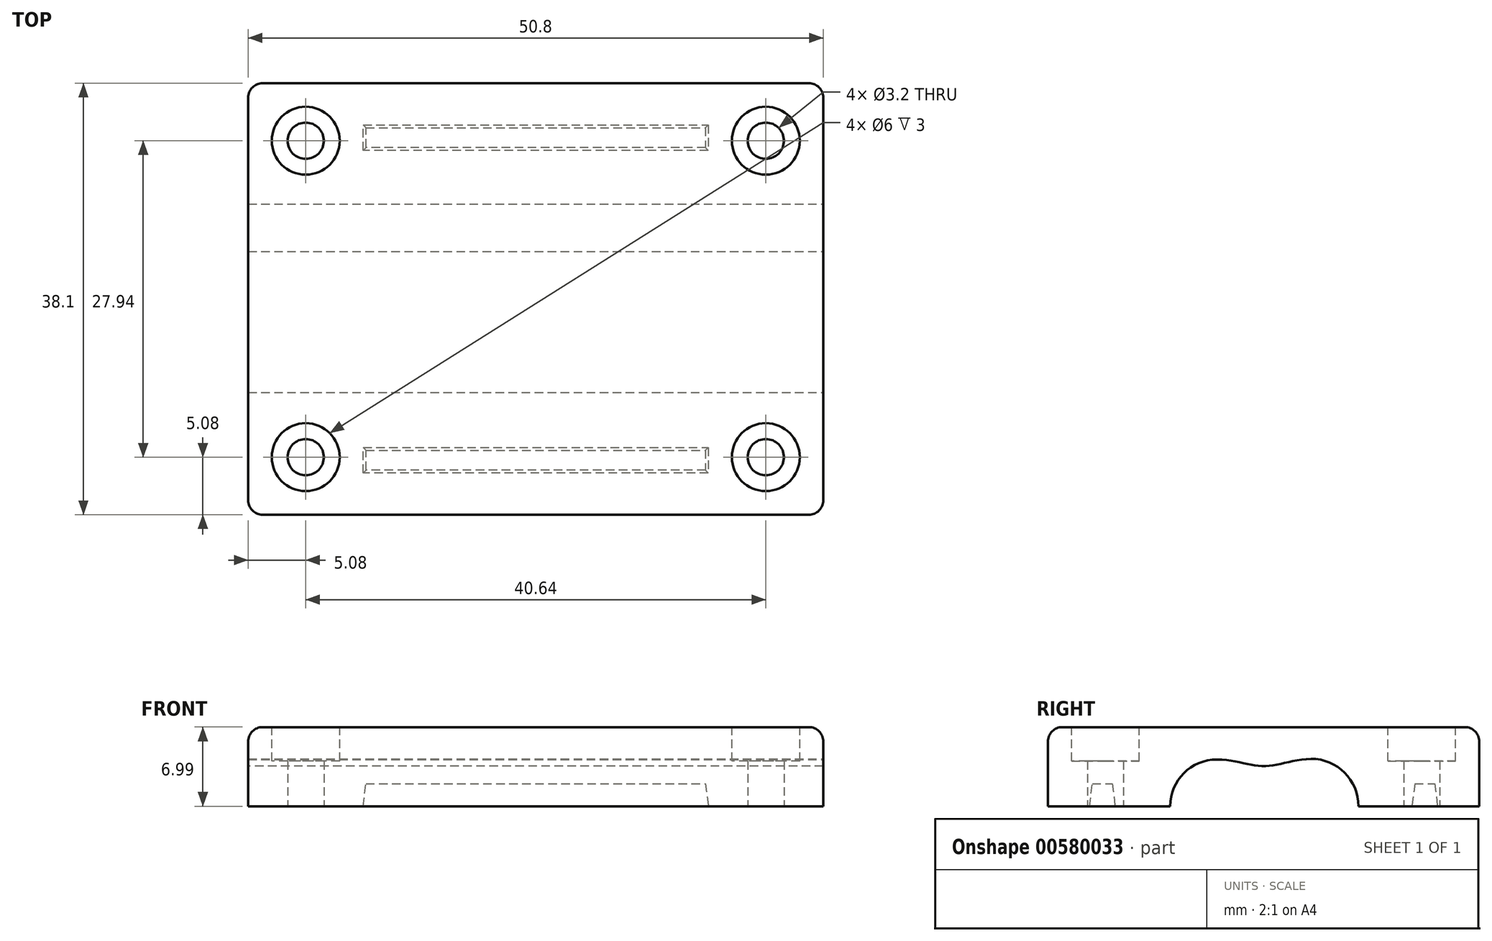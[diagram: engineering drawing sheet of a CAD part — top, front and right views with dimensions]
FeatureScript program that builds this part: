
annotation { "Feature Type Name" : "Feature", "Feature Type Description" : "" }
export const myFeature = defineFeature(function(context is Context, id is Id, definition is map)
    precondition{}
    {
        {
            var Q0;
            Q0=qCreatedBy(makeId("Top.planeOp"),FACE);
            var sketch = newSketch(context, id + "F0", { "sketchPlane" : qUnion([Q0])});
            skLineSegment(sketch, "E0.bottom", {"start": v(-38.1, 0) * mm, "end": v(38.1, 0) * mm});
            skLineSegment(sketch, "E0.top", {"start": v(-38.1, -4.13) * mm, "end": v(38.1, -4.13) * mm});
            skLineSegment(sketch, "E0.left", {"start": v(-38.1, 0) * mm, "end": v(-38.1, -4.13) * mm});
            skLineSegment(sketch, "E0.right", {"start": v(38.1, 0) * mm, "end": v(38.1, -4.13) * mm});
            skLineSegment(sketch, "E1.top", {"start": v(-38.1, 4.2) * mm, "end": v(38.1, 4.2) * mm});
            skLineSegment(sketch, "E1.left", {"start": v(-38.1, 0) * mm, "end": v(-38.1, 4.2) * mm});
            skLineSegment(sketch, "E1.right", {"start": v(38.1, 0) * mm, "end": v(38.1, 4.2) * mm});
            skLineSegment(sketch, "E2.MirrorCS", {"start": v(38.1, 8.38) * mm, "end": v(38.1, 4.2) * mm});
            skLineSegment(sketch, "E3.MirrorCS", {"start": v(-38.1, 8.38) * mm, "end": v(38.1, 8.38) * mm});
            skLineSegment(sketch, "E4.MirrorCS", {"start": v(-38.1, 8.38) * mm, "end": v(-38.1, 4.2) * mm});
            skLineSegment(sketch, "E5.MirrorCS", {"start": v(38.1, -8.25) * mm, "end": v(38.1, -4.12) * mm});
            skLineSegment(sketch, "E6.MirrorCS", {"start": v(-38.1, -8.25) * mm, "end": v(38.1, -8.25) * mm});
            skLineSegment(sketch, "E7.MirrorCS", {"start": v(-38.1, -8.25) * mm, "end": v(-38.1, -4.12) * mm});
            skSolve(sketch);
        }
        {
            var Q0;
            Q0=qCreatedBy(makeId("Top.planeOp"),FACE);
            var sketch = newSketch(context, id + "F1", { "sketchPlane" : qUnion([Q0])});
            skLineSegment(sketch, "E8.bottom", {"start": v(-25.4, 19.05) * mm, "end": v(25.4, 19.05) * mm});
            skLineSegment(sketch, "E8.top", {"start": v(-25.4, -19.05) * mm, "end": v(25.4, -19.05) * mm});
            skLineSegment(sketch, "E8.left", {"start": v(-25.4, 19.05) * mm, "end": v(-25.4, -19.05) * mm});
            skLineSegment(sketch, "E8.right", {"start": v(25.4, 19.05) * mm, "end": v(25.4, -19.05) * mm});
            skSolve(sketch);
        }
        {
            var Q0;
            Q0=qSketchRegion(id+"F1",true);
            extrude(context, id + "F2", {"entities" : qUnion([Q0]), "oppositeDirection" : true, "depth" : 0 * mm, "offsetDistance" : 25.4 * mm, "hasSecondDirection" : true, "secondDirectionOppositeDirection" : false, "secondDirectionDepth" : 7 * mm});
        }
        {
            var Q0;
            Q0=makeQuery(id+"F2.opExtrude","SWEPT_FACE",FACE,{"disambiguationData":[OSD([sQuery(id+"F1.wireOp",EDGE,"E8.right")])]});
            var sketch = newSketch(context, id + "F3", { "sketchPlane" : qUnion([Q0])});
            skLineSegment(sketch, "E9.0", {"start": v(-8.25, 0) * mm, "end": v(-4.12, 0) * mm});
            skLineSegment(sketch, "E10.0", {"start": v(8.38, 0) * mm, "end": v(4.2, 0) * mm});
            skArc(sketch, "E11", {"start": v(-4.13, 4.13) * mm, "mid": v(-8.25, 0) * mm, "end": v(-4.12, -4.13) * mm});
            skArc(sketch, "E12", {"start": v(4.2, -4.2) * mm, "mid": v(8.38, 0) * mm, "end": v(4.2, 4.2) * mm});
            skFitSpline(sketch, "E13", {"points": [v(-4.12, 4.13) * mm, v(0, 3.54) * mm, v(4.2, 4.2) * mm], "startDerivative": vector(10.24, -0.07) * mm, "endDerivative": vector(9.95, 0.46) * mm});
            skFitSpline(sketch, "E14", {"points": [v(-4.12, -4.13) * mm, v(0, -3.63) * mm, v(4.2, -4.2) * mm], "startDerivative": vector(7.18, -0.46) * mm, "endDerivative": vector(12.23, 0.06) * mm});
            skSolve(sketch);
        }
        {
            var Q0;
            Q0=qSketchRegion(id+"F3",true);
            var Q1;
            Q1=makeQuery(id+"F2.opExtrude","SWEPT_FACE",FACE,{"disambiguationData":[OSD([sQuery(id+"F1.wireOp",EDGE,"E8.left")])]});
            extrude(context, id + "F4", {"entities" : qUnion([Q0]), "operationType" : NewBodyOperationType.REMOVE, "endBound" : BoundingType.UP_TO_SURFACE, "oppositeDirection" : true, "depth" : 25.4 * mm, "endBoundEntityFace" : qUnion([Q1]), "offsetDistance" : 25.4 * mm});
        }
        {
            var Q0;
            Q0=makeQuery(id+"Fef220ugahAK9jw_1.boolean.opBoolean","MERGE",FACE,{"derivedFrom":[makeQuery(id+"F2.opExtrude","CAP_FACE",FACE,{"disambiguationData":[OSD([sQuery(id+"F1.wireOp",EDGE,"E8.bottom"),sQuery(id+"F1.wireOp",EDGE,"E8.top"),sQuery(id+"F1.wireOp",EDGE,"E8.left"),sQuery(id+"F1.wireOp",EDGE,"E8.right")])],"isStart":false}),makeQuery(id+"Fef220ugahAK9jw_1.opExtrude","SWEPT_FACE",FACE,{"disambiguationData":[OSD([sQuery(id+"FHLQYaHWqDmCoNx_1.wireOp",EDGE,"rQF1xo6v-WYjC-psFk-ypBl-txbA0QUANmOA.bottom")])]})]});
            var sketch = newSketch(context, id + "F5", { "sketchPlane" : qUnion([Q0])});
            skCircle(sketch, "E15", {"center": v(20.32, -13.97) * mm, "radius": 1.6 * mm});
            skCircle(sketch, "E16.MirrorC", {"center": v(-20.32, -13.97) * mm, "radius": 1.6 * mm});
            skCircle(sketch, "E17.MirrorC", {"center": v(-20.32, 13.97) * mm, "radius": 1.6 * mm});
            skCircle(sketch, "E18.MirrorC", {"center": v(20.32, 13.97) * mm, "radius": 1.6 * mm});
            skSolve(sketch);
        }
        {
            var Q0;
            Q0=qSketchRegion(id+"F5",true);
            extrude(context, id + "F6", {"entities" : qUnion([Q0]), "operationType" : NewBodyOperationType.REMOVE, "oppositeDirection" : true, "depth" : 25.4 * mm, "offsetDistance" : 25.4 * mm});
        }
        {
            var Q0;
            Q0=qCreatedBy(makeId("Top.planeOp"),FACE);
            var sketch = newSketch(context, id + "F7", { "sketchPlane" : qUnion([Q0])});
            skLineSegment(sketch, "E19.bottom", {"start": v(-15.24, 15.37) * mm, "end": v(15.24, 15.37) * mm});
            skLineSegment(sketch, "E19.top", {"start": v(-15.24, 13.11) * mm, "end": v(15.24, 13.11) * mm});
            skLineSegment(sketch, "E19.left", {"start": v(-15.24, 15.37) * mm, "end": v(-15.24, 13.11) * mm});
            skLineSegment(sketch, "E19.right", {"start": v(15.24, 15.37) * mm, "end": v(15.24, 13.11) * mm});
            skLineSegment(sketch, "E20.MirrorCS", {"start": v(-15.24, -15.37) * mm, "end": v(-15.24, -13.11) * mm});
            skLineSegment(sketch, "E21.MirrorCS", {"start": v(15.24, -15.37) * mm, "end": v(15.24, -13.11) * mm});
            skLineSegment(sketch, "E22.MirrorCS", {"start": v(-15.24, -15.37) * mm, "end": v(15.24, -15.36) * mm});
            skLineSegment(sketch, "E23.MirrorCS", {"start": v(-15.24, -13.11) * mm, "end": v(15.24, -13.11) * mm});
            skSolve(sketch);
        }
        {
            var Q0;
            Q0=qSketchRegion(id+"F7",true);
            extrude(context, id + "F8", {"entities" : qUnion([Q0]), "operationType" : NewBodyOperationType.REMOVE, "depth" : 2 * mm, "offsetDistance" : 25.4 * mm, "hasDraft" : true, "draftAngle" : 7 * degree, "draftPullDirection" : true});
        }
        {
            var Q0;
            Q0=makeQuery(id+"F2.opExtrude","CAP_EDGE",EDGE,{"disambiguationData":[OSD([sQuery(id+"F1.wireOp",EDGE,"E8.right")])],"isStart":true});
            var Q1;
            Q1=makeQuery(id+"F2.opExtrude","CAP_EDGE",EDGE,{"disambiguationData":[OSD([sQuery(id+"F1.wireOp",EDGE,"E8.bottom")])],"isStart":true});
            var Q2;
            Q2=makeQuery(id+"F2.opExtrude","SWEPT_EDGE",EDGE,{"disambiguationData":[OSD([sQuery(id+"F1.wireOp",EDGE,"E8.bottom"),sQuery(id+"F1.wireOp",EDGE,"E8.right")])]});
            var Q3;
            Q3=makeQuery(id+"F2.opExtrude","CAP_EDGE",EDGE,{"disambiguationData":[OSD([sQuery(id+"F1.wireOp",EDGE,"E8.top")])],"isStart":true});
            var Q4;
            Q4=makeQuery(id+"F2.opExtrude","CAP_EDGE",EDGE,{"disambiguationData":[OSD([sQuery(id+"F1.wireOp",EDGE,"E8.left")])],"isStart":true});
            var Q5;
            Q5=makeQuery(id+"F2.opExtrude","SWEPT_EDGE",EDGE,{"disambiguationData":[OSD([sQuery(id+"F1.wireOp",EDGE,"E8.bottom"),sQuery(id+"F1.wireOp",EDGE,"E8.left")])]});
            var Q6;
            Q6=makeQuery(id+"F2.opExtrude","SWEPT_EDGE",EDGE,{"disambiguationData":[OSD([sQuery(id+"F1.wireOp",EDGE,"E8.top"),sQuery(id+"F1.wireOp",EDGE,"E8.left")])]});
            var Q7;
            Q7=makeQuery(id+"F2.opExtrude","SWEPT_EDGE",EDGE,{"disambiguationData":[OSD([sQuery(id+"F1.wireOp",EDGE,"E8.top"),sQuery(id+"F1.wireOp",EDGE,"E8.right")])]});
            fillet(context, id + "F9", {"entities" : qUnion([Q0, Q1, Q2, Q3, Q4, Q5, Q6, Q7]), "radius" : 1.27 * mm, "tangentPropagation" : true, "allowEdgeOverflow" : false});
        }
        {
            var Q0;
            Q0=makeQuery(id+"F2.opExtrude","CAP_FACE",FACE,{"disambiguationData":[OSD([sQuery(id+"F1.wireOp",EDGE,"E8.bottom"),sQuery(id+"F1.wireOp",EDGE,"E8.top"),sQuery(id+"F1.wireOp",EDGE,"E8.left"),sQuery(id+"F1.wireOp",EDGE,"E8.right")])],"isStart":true});
            var sketch = newSketch(context, id + "F10", { "sketchPlane" : qUnion([Q0])});
            skCircle(sketch, "E24", {"center": v(-20.32, 13.97) * mm, "radius": 3 * mm});
            skCircle(sketch, "E25.MirrorC", {"center": v(20.32, 13.97) * mm, "radius": 3 * mm});
            skCircle(sketch, "E26.MirrorC", {"center": v(-20.32, -13.97) * mm, "radius": 3 * mm});
            skCircle(sketch, "E27.MirrorC", {"center": v(20.32, -13.97) * mm, "radius": 3 * mm});
            skSolve(sketch);
        }
        {
            var Q0;
            Q0 = qSketchRegion(id + "F10", true);
            extrude(context, id + "F11", {"entities" : qUnion([Q0]), "operationType" : NewBodyOperationType.REMOVE, "oppositeDirection" : true, "depth" : 3 * mm, "offsetDistance" : 25.4 * mm});
        }
    });
